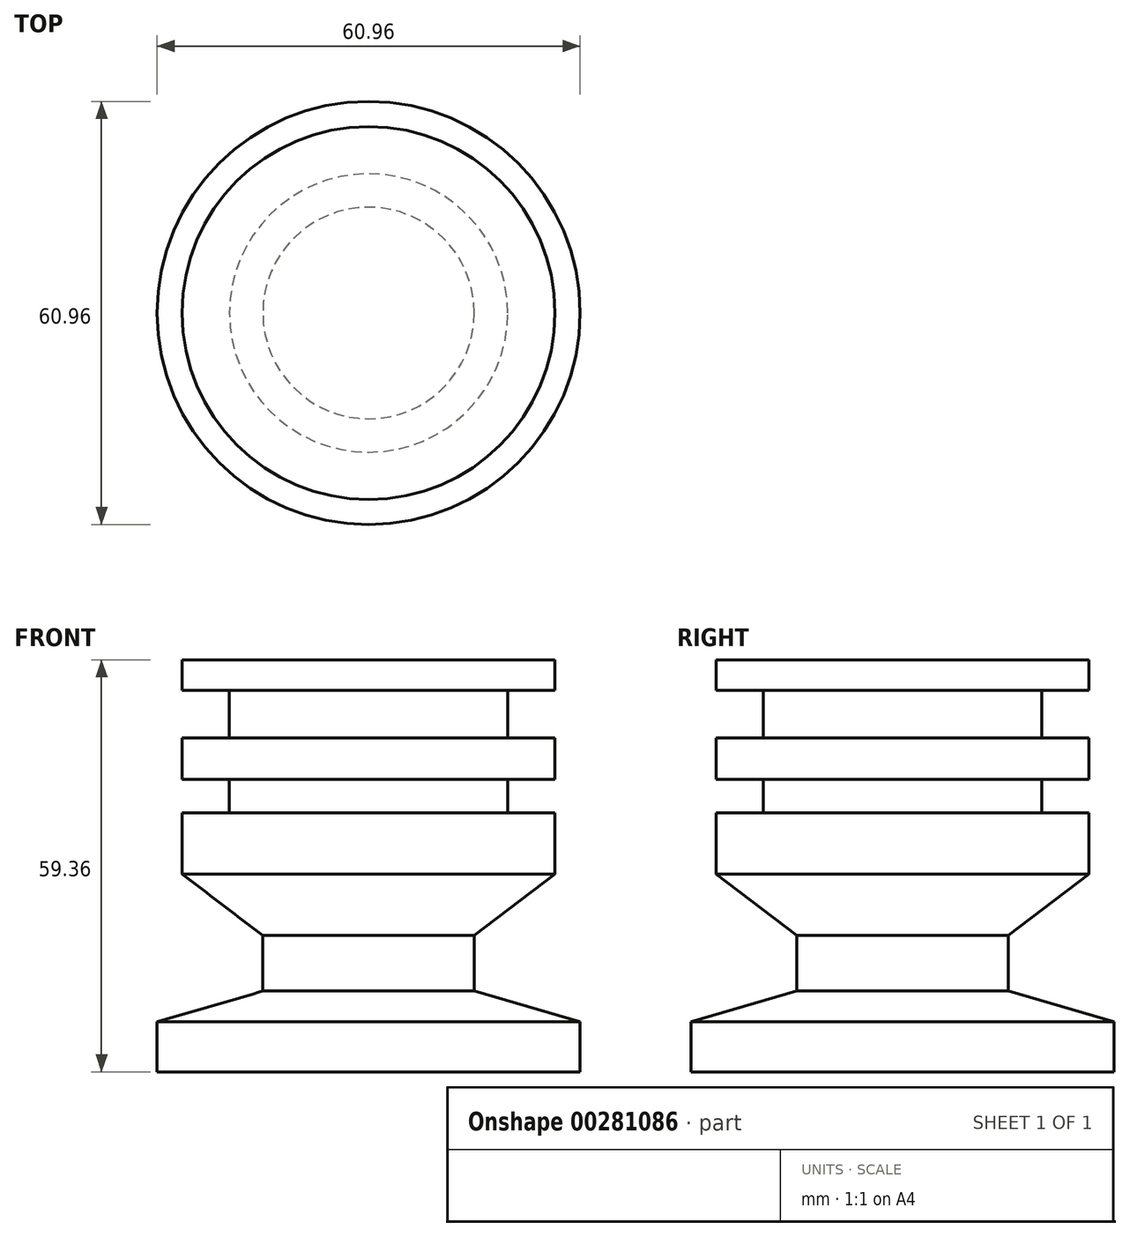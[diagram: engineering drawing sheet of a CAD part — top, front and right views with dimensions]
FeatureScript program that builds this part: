
annotation { "Feature Type Name" : "Feature", "Feature Type Description" : "" }
export const myFeature = defineFeature(function(context is Context, id is Id, definition is map)
    precondition{}
    {
        {
            var Q0;
            Q0=qCreatedBy(makeId("Front.planeOp"),FACE);
            var sketch = newSketch(context, id + "F0", { "sketchPlane" : qUnion([Q0])});
            skLineSegment(sketch, "E0", {"start": v(0, 84.23) * mm, "end": v(0, -108.7) * mm, "construction": true});
            skSolve(sketch);
        }
        {
            var Q0;
            Q0=qCreatedBy(makeId("Front.planeOp"),FACE);
            var sketch = newSketch(context, id + "F1", { "sketchPlane" : qUnion([Q0])});
            skLineSegment(sketch, "E1", {"start": v(0, -59.36) * mm, "end": v(-30.48, -59.36) * mm});
            skLineSegment(sketch, "E2", {"start": v(-30.48, -59.36) * mm, "end": v(-30.48, -52.14) * mm});
            skLineSegment(sketch, "E3", {"start": v(-30.48, -52.14) * mm, "end": v(-15.24, -47.73) * mm});
            skLineSegment(sketch, "E4", {"start": v(-15.24, -47.73) * mm, "end": v(-15.24, -39.7) * mm});
            skLineSegment(sketch, "E5", {"start": v(-15.24, -39.7) * mm, "end": v(-26.87, -30.88) * mm});
            skLineSegment(sketch, "E6", {"start": v(-26.87, -30.88) * mm, "end": v(-26.87, -22.06) * mm});
            skLineSegment(sketch, "E7", {"start": v(-26.87, -22.06) * mm, "end": v(-20.05, -22.06) * mm});
            skLineSegment(sketch, "E8", {"start": v(-20.05, -22.06) * mm, "end": v(-20.05, -17.25) * mm});
            skLineSegment(sketch, "E9", {"start": v(-20.05, -17.25) * mm, "end": v(-26.87, -17.25) * mm});
            skLineSegment(sketch, "E10", {"start": v(-26.87, -17.25) * mm, "end": v(-26.87, -11.23) * mm});
            skLineSegment(sketch, "E11", {"start": v(-26.87, -11.23) * mm, "end": v(-20.05, -11.23) * mm});
            skLineSegment(sketch, "E12", {"start": v(-20.05, -11.23) * mm, "end": v(-20.05, -4.41) * mm});
            skLineSegment(sketch, "E13", {"start": v(-20.05, -4.41) * mm, "end": v(-26.87, -4.41) * mm});
            skLineSegment(sketch, "E14", {"start": v(-26.87, -4.41) * mm, "end": v(-26.87, 0) * mm});
            skLineSegment(sketch, "E15", {"start": v(-26.87, 0) * mm, "end": v(-20.05, 0) * mm});
            skLineSegment(sketch, "E16", {"start": v(-20.05, 0) * mm, "end": v(0, 0) * mm});
            skSolve(sketch);
        }
        {
            var Q0;
            Q0 = qConstructionFilter(qBodyType(qCreatedBy(id + "F1" ,EDGE), BodyType.WIRE), ConstructionObject.NO);
            var Q1;
            Q1=sQuery(id+"F0.wireOp",EDGE,"E0");
            revolve(context, id + "F2", {"bodyType" : ToolBodyType.SURFACE, "surfaceEntities" : qUnion([Q0]), "axis" : qUnion([Q1]), "revolveType" : RevolveType.FULL});
        }
    });
